# Revit family: Gira_016930
name_source: partatom
category: Electrical Fixtures
revit_build: Autodesk Revit 2017 (Build: 20160225_1515(x64)
units: mm (PartAtom-declared; Revit-internal decimal feet)

## family parameters
Cut with Voids When Loaded = No
Host = Face
Maintain Annotation Orientation = No
Part Type = Normal
Room Calculation Point = No
Round Connector Dimension = Use Diameter
Shared = No

## types (1)
- Light sig. E10/E14 bayonet WP SM grey
    Application as button = no
    Assembly arrangement = Complete device
    BIM = https://media.live.bim.site
    BIMSITE_PRODUCT_ID = bb5a4735bf759ccacf21f47db4f7e615c281f6a8
    Colour = Grey
    Cost = 0 $
    Default Elevation = 1219 mm
    Description = Light sig.E10 E14 bayon. WP SM GY Light signal E10 or E14 with bayonet lock,grey Notes : - The following devices are delivered without mounting plate. - Not suitable for continuous operation. - After removing the reducing piece, the light signal E 10 can be used as light signal E 14.
    GTIN = 4010337169307
    HAN = 016930
    Halogen free = No
    HeinzeBIM = https://www.heinze.de
    Lamp holder = Sonstige (*de-DE)
    Manufacturer = Gira
    Material = plastic
    Material quality = Thermoplastic
    Suitable for degree of protection (IP) = IP44
    Surface protection = Sonstige (*de-DE)
    Transparent = No
    URL = https://www.gira.de
    With exchangeable symbol = No
    With fixed symbol/imprint = No
    With flashlight = No
    With light source = No

## geometry (parser evidence)
native form markers: Blend x2, Sweep x11
no freeform markers — native parametric forms only
